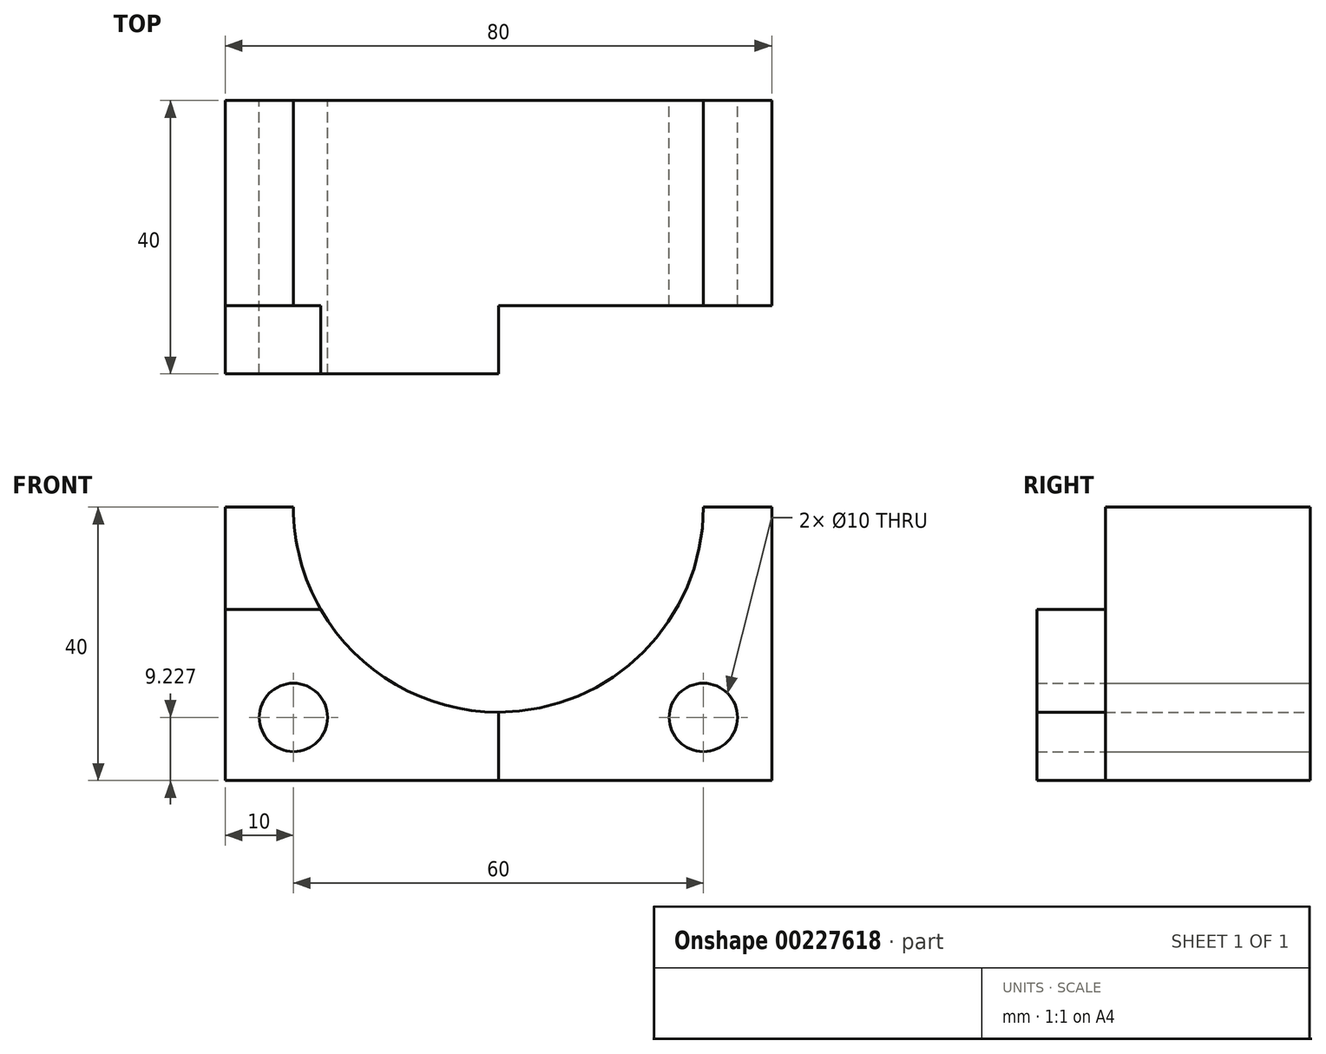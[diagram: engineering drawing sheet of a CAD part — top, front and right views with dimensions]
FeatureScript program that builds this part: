
annotation { "Feature Type Name" : "Feature", "Feature Type Description" : "" }
export const myFeature = defineFeature(function(context is Context, id is Id, definition is map)
    precondition{}
    {
        {
            var Q0;
            Q0=qCreatedBy(makeId("Front.planeOp"),FACE);
            var sketch = newSketch(context, id + "F0", { "sketchPlane" : qUnion([Q0])});
            skArc(sketch, "E0", {"start": v(-30, 0) * mm, "mid": v(0, -30) * mm, "end": v(30, 0) * mm});
            skLineSegment(sketch, "E1", {"start": v(-30, 0) * mm, "end": v(-40, 0) * mm});
            skLineSegment(sketch, "E2", {"start": v(-40, 0) * mm, "end": v(-40, -40) * mm});
            skLineSegment(sketch, "E3", {"start": v(-40, -40) * mm, "end": v(40, -40) * mm});
            skLineSegment(sketch, "E4", {"start": v(40, -40) * mm, "end": v(40, 0) * mm});
            skLineSegment(sketch, "E5", {"start": v(40, 0) * mm, "end": v(30, 0) * mm});
            skLineSegment(sketch, "E6", {"start": v(-40, -15) * mm, "end": v(-25.98, -15) * mm});
            skCircle(sketch, "E7", {"center": v(-30, -30.77) * mm, "radius": 5 * mm});
            skCircle(sketch, "E8", {"center": v(30, -30.77) * mm, "radius": 5 * mm});
            skLineSegment(sketch, "E9", {"start": v(0, -30) * mm, "end": v(0, -40) * mm});
            skSolve(sketch);
        }
        {
            var Q0;
            {var subQ3=sQuery(id+"F0.wireOp",EDGE,"E4");Q0=makeQuery(id+"F0.imprint","IMPRINT",FACE,{"disambiguationData":[TD([[makeQuery(id+"F0.imprint","IMPRINT",EDGE,{"derivedFrom":subQ3}),1.0]])]});}
            var Q1;
            {var subQ0=sQuery(id+"F0.wireOp",EDGE,"E1");Q1=makeQuery(id+"F0.imprint","IMPRINT",FACE,{"disambiguationData":[TD([[makeQuery(id+"F0.imprint","IMPRINT",EDGE,{"derivedFrom":subQ0}),1.0]])]});}
            extrude(context, id + "F1", {"entities" : qUnion([Q0, Q1]), "depth" : 30 * mm});
        }
        {
            var Q0;
            {var subQ0=sQuery(id+"F0.wireOp",EDGE,"E6");Q0=makeQuery(id+"F0.imprint","IMPRINT",FACE,{"disambiguationData":[TD([[makeQuery(id+"F0.imprint","IMPRINT",EDGE,{"derivedFrom":subQ0}),-1.0]])]});}
            extrude(context, id + "F2", {"entities" : qUnion([Q0]), "operationType" : NewBodyOperationType.ADD, "depth" : 40 * mm});
        }
    });
